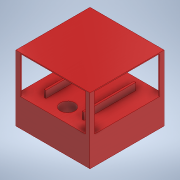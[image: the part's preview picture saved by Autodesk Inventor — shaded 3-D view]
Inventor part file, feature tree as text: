
AUTODESK INVENTOR PART (.ipt)
format: ipt  version: 2020 (Build 240168000, 168)  size: 196,608 bytes
history: native  units: mm
features: extrude x5, sketch x5, other x2, plane x2
ambient origin geometry x8: Origin, YZ Plane, XZ Plane, XY Plane, X Axis, Y Axis, Z Axis, Center Point
bodies: Body1 (feature_tree)
feature tree (14):
  other  "Sólido1"
  extrude  "Extrusión1"  Depth=200.0mm
  extrude  "Extrusión2"  Depth=150.0mm TaperAngle=0.0deg
  other  "Eje de trabajo1"
  extrude  "Extrusión3"  Depth=60.0mm
  extrude  "Extrusión4"  Depth=60.0mm
  extrude  "Extrusión5"  Depth=280.0mm
  sketch  "Boceto1"  dims[d0=400.0mm d2=200.0mm]
  sketch  "Boceto3"  dims[d3=200.0mm d4=150.0mm d5=0.0mm]
  plane  "Plano de trabajo1"
  plane  "Plano de trabajo2"
  sketch  "Boceto4"  dims[d7=153.75mm d8=0.0mm d13=60.0mm]
  sketch  "Boceto5"  dims[d14=280.0mm d15=60.0mm]
  sketch  "Boceto6"  dims[d19=10.0mm d20=280.0mm d21=97.5mm d22=10.0mm d23=280.0mm d24=97.5mm d25=38.0mm d26=0.0mm d27=79.0mm d28=25.0mm d29=5.0mm d30=20.0mm d31=20.0mm d32=25.0mm d33=5.0mm d34=20.0mm d35=20.0mm d36=25.0mm d37=5.0mm d38=20.0mm d39=20.0mm d40=25.0mm d41=5.0mm d42=20.0mm d43=20.0mm d44=200.0mm d45=0.0mm d46=5.0mm d47=0.0mm]
